# Revit family: REVIT-PVIFX-LI2017
name_source: partatom
category: Mechanical Equipment
revit_build: Autodesk Revit 2017 (Build: 20190507_1515(x64)
units: mm (PartAtom-declared; Revit-internal decimal feet)

## family parameters
Always vertical = Yes
Cut with Voids When Loaded = No
Part Type = Normal
Room Calculation Point = No
Round Connector Dimension = Use Radius
Shared = No
Work Plane-Based = No

## types (2) — shared parameters
Air Inlet Angle = 33.00°
Air Inlet Diameter = 6"
Air Inlet Extension = 24"
Air Inlet Height = 80"
Air Inlet Radius = 3"
Apparent Load = 1560 VA
Assembly Code = D3020100
Building Return NPT = 2"
Building Return Radius = 1"
Cold Inlet Extension = 34 3/4"
Cold Inlet Height = 6"
Cold Inlet NPT = 2 1/2"
Cold Inlet Radius = 1 1/4"
Condensate Connection = 3/4"
Condensate Connection Radius = 3/8"
Condensate Extension = 43 7/16"
Control Panel Extension = 29 1/2"
Current = 13 A
Description = POWER VT® Plus Condensing Water Heater
Disclaimer = This rendering is for building modeling purposes only. Submittal/catalog is still the contract document. PVI reserves the right to change design and specification without notice.
Drain Extension = 26 3/8"
Drain Height = 21 7/8"
Drain NPT = 1"
Drain Radius = 1/2"
Front Skid = 22 1/2"
Gas Inlet NPT = 1"
Gas Inlet Radius = 1/2"
Gas Train Extension = 25 13/16"
Gas Train Height = 80"
Hot Outlet Extension = 27"
Hot Outlet Height = 68"
Hot Outlet NPT = 2"
Hot Outlet Radius = 1"
Manufacturer = PVI Industries, LLC
Recirculation Height = 33 1/2"
Relief Extension = 23 1/2"
Relief Height = 68 1/8"
Relief NPT = 1"
Relief Radius = 1/2"
Skid Length = 64"
Skid Spacing = 24 11/16"
URL = www.pvi.com
Unit Height = 88"
Unit Radius = 22 1/2"
Vent Angle = 0.00°
Vent Diameter = 6 5/8"
Vent Extension = 40 3/16"
Vent Height = 7"
Vent Radius = 3 5/16"

## per-type parameters (varying)
| type | Input | Recovery Rate 40F to 140F (gph) | Weight |
| 50 LX 300A-PVIF | 500000 Btu/h | 588 | 1920 |
| 75 LX 300A-PVIF | 750000 Btu/h | 882 | 2110 |

note: column(s) folded — value = type name in every type: Model

## geometry (parser evidence)
native form markers: Blend x2, Sweep x3
no freeform markers — native parametric forms only
